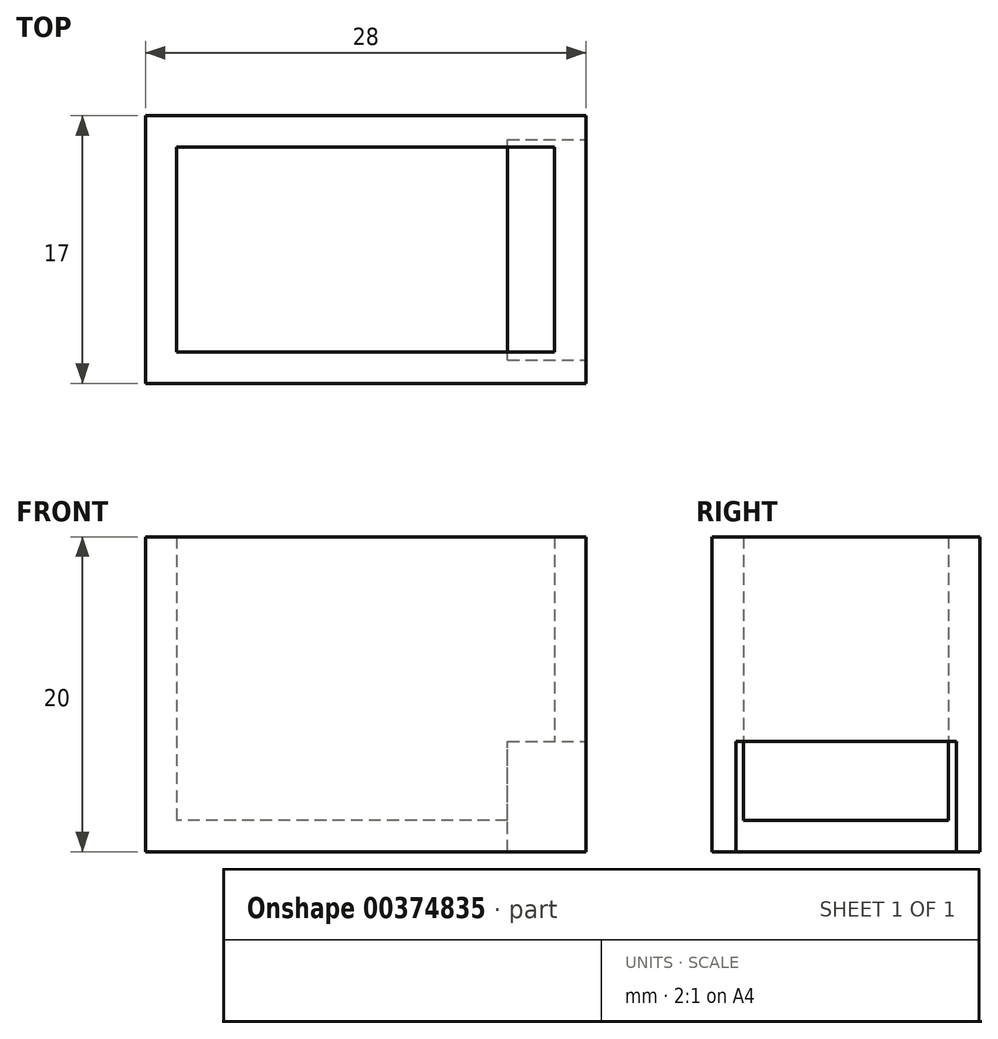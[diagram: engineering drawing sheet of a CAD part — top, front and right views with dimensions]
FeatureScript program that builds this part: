
annotation { "Feature Type Name" : "Feature", "Feature Type Description" : "" }
export const myFeature = defineFeature(function(context is Context, id is Id, definition is map)
    precondition{}
    {
        {
            var Q0;
            Q0=qCreatedBy(makeId("Top.planeOp"),FACE);
            var sketch = newSketch(context, id + "F0", { "sketchPlane" : qUnion([Q0])});
            skLineSegment(sketch, "E0.bottom", {"start": v(14, -8.5) * mm, "end": v(-14, -8.5) * mm});
            skLineSegment(sketch, "E0.top", {"start": v(14, 8.5) * mm, "end": v(-14, 8.5) * mm});
            skLineSegment(sketch, "E0.left", {"start": v(14, -8.5) * mm, "end": v(14, 8.5) * mm});
            skLineSegment(sketch, "E0.right", {"start": v(-14, -8.5) * mm, "end": v(-14, 8.5) * mm});
            skPoint(sketch, "E0.middle", {"position": v(0, 0) * mm});
            skSolve(sketch);
        }
        {
            var Q0;
            Q0 = qSketchRegion(id + "F0", true);
            extrude(context, id + "F1", {"entities" : qUnion([Q0]), "depth" : 20 * mm, "offsetDistance" : 25 * mm});
        }
        {
            var Q0;
            Q0=makeQuery(id+"F1.opExtrude","CAP_FACE",FACE,{"disambiguationData":[OSD([sQuery(id+"F0.wireOp",EDGE,"E0.bottom"),sQuery(id+"F0.wireOp",EDGE,"E0.top"),sQuery(id+"F0.wireOp",EDGE,"E0.left"),sQuery(id+"F0.wireOp",EDGE,"E0.right")])],"isStart":false});
            shell(context, id + "F2", {"entities" : qUnion([Q0]), "thickness" : 2 * mm});
        }
        {
            var Q0;
            Q0=makeQuery(id+"F1.opExtrude","SWEPT_FACE",FACE,{"disambiguationData":[OSD([sQuery(id+"F0.wireOp",EDGE,"E0.left")])]});
            var sketch = newSketch(context, id + "F3", { "sketchPlane" : qUnion([Q0])});
            skLineSegment(sketch, "E1.bottom", {"start": v(-7, 0) * mm, "end": v(7, 0) * mm});
            skLineSegment(sketch, "E1.top", {"start": v(-7, 5) * mm, "end": v(7, 5) * mm});
            skLineSegment(sketch, "E1.left", {"start": v(-7, 0) * mm, "end": v(-7, 5) * mm});
            skLineSegment(sketch, "E1.right", {"start": v(7, 0) * mm, "end": v(7, 5) * mm});
            skSolve(sketch);
        }
        {
            var Q0;
            Q0 = qSketchRegion(id + "F3", true);
            extrude(context, id + "F4", {"entities" : qUnion([Q0]), "operationType" : NewBodyOperationType.REMOVE, "oppositeDirection" : true, "depth" : 5 * mm, "offsetDistance" : 25 * mm});
        }
        {
            var Q0;
            Q0=makeQuery(id+"F4.boolean.opBoolean","COPY",FACE,{"derivedFrom":makeQuery(id+"F4.opExtrude","SWEPT_FACE",FACE,{"disambiguationData":[OSD([sQuery(id+"F3.wireOp",EDGE,"E1.top")])]})});
            extrude(context, id + "F5", {"entities" : qUnion([Q0]), "operationType" : NewBodyOperationType.REMOVE, "oppositeDirection" : true, "depth" : 2 * mm, "offsetDistance" : 25 * mm});
        }
    });
